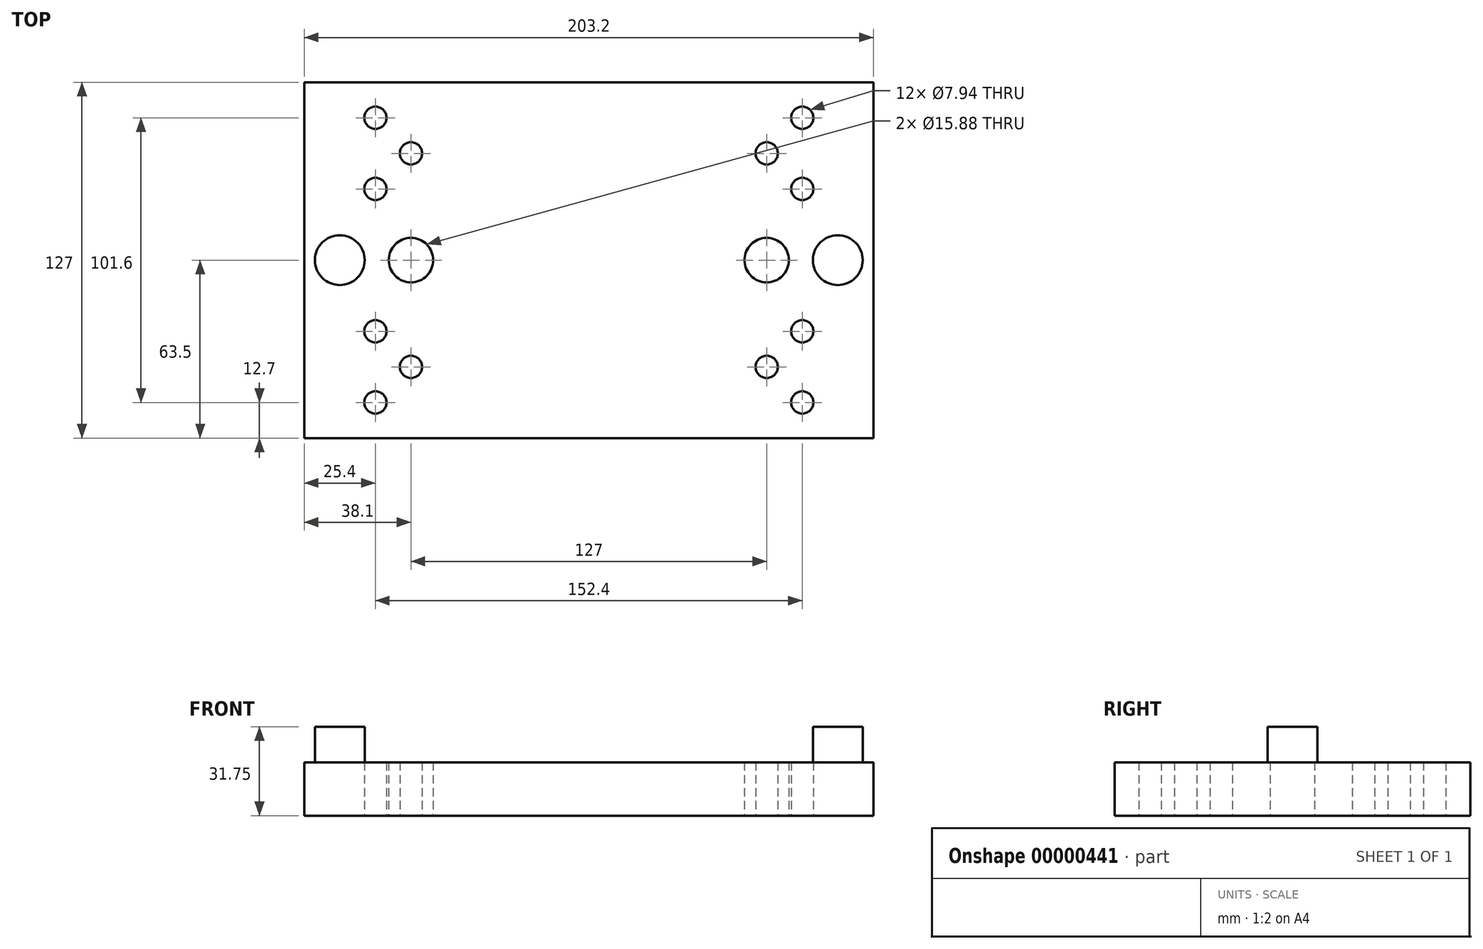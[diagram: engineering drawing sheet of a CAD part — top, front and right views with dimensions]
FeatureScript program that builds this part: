
annotation { "Feature Type Name" : "Feature", "Feature Type Description" : "" }
export const myFeature = defineFeature(function(context is Context, id is Id, definition is map)
    precondition{}
    {
        {
            var Q0;
            Q0=qCreatedBy(makeId("Top.planeOp"),FACE);
            var sketch = newSketch(context, id + "F0", { "sketchPlane" : qUnion([Q0])});
            skLineSegment(sketch, "E0.bottom", {"start": v(0, 0) * mm, "end": v(203.2, 0) * mm});
            skLineSegment(sketch, "E0.top", {"start": v(0, 127) * mm, "end": v(203.2, 127) * mm});
            skLineSegment(sketch, "E0.left", {"start": v(0, 0) * mm, "end": v(0, 127) * mm});
            skLineSegment(sketch, "E0.right", {"start": v(203.2, 0) * mm, "end": v(203.2, 127) * mm});
            skCircle(sketch, "E1", {"center": v(38.1, 63.5) * mm, "radius": 7.94 * mm});
            skCircle(sketch, "E2", {"center": v(165.1, 63.5) * mm, "radius": 7.94 * mm});
            skCircle(sketch, "E3", {"center": v(177.8, 114.3) * mm, "radius": 3.97 * mm});
            skCircle(sketch, "E4", {"center": v(165.1, 101.6) * mm, "radius": 3.97 * mm});
            skCircle(sketch, "E5", {"center": v(177.8, 88.9) * mm, "radius": 3.97 * mm});
            skCircle(sketch, "E6", {"center": v(177.8, 38.1) * mm, "radius": 3.97 * mm});
            skCircle(sketch, "E7", {"center": v(165.1, 25.4) * mm, "radius": 3.97 * mm});
            skCircle(sketch, "E8", {"center": v(177.8, 12.7) * mm, "radius": 3.97 * mm});
            skCircle(sketch, "E9", {"center": v(25.4, 38.1) * mm, "radius": 3.97 * mm});
            skCircle(sketch, "E10", {"center": v(38.1, 25.4) * mm, "radius": 3.97 * mm});
            skCircle(sketch, "E11", {"center": v(25.4, 12.7) * mm, "radius": 3.97 * mm});
            skCircle(sketch, "E12", {"center": v(25.4, 114.3) * mm, "radius": 3.97 * mm});
            skCircle(sketch, "E13", {"center": v(38.1, 101.6) * mm, "radius": 3.97 * mm});
            skCircle(sketch, "E14", {"center": v(25.4, 88.9) * mm, "radius": 3.97 * mm});
            skSolve(sketch);
        }
        {
            var Q0;
            Q0=makeQuery(id+"F0.imprint","IMPRINT",FACE,{"disambiguationData":[TD([[makeQuery(id+"F0.imprint","IMPRINT",EDGE,{"derivedFrom":sQuery(id+"F0.wireOp",EDGE,"E0.bottom")}),1.0]])]});
            extrude(context, id + "F1", {"entities" : qUnion([Q0]), "depth" : 19.05 * mm});
        }
        {
            var Q0;
            Q0=makeQuery(id+"F1.opExtrude","CAP_FACE",FACE,{"disambiguationData":[OSD([sQuery(id+"F0.wireOp",EDGE,"E0.bottom"),sQuery(id+"F0.wireOp",EDGE,"E0.top"),sQuery(id+"F0.wireOp",EDGE,"E0.left"),sQuery(id+"F0.wireOp",EDGE,"E0.right"),sQuery(id+"F0.wireOp",EDGE,"E1"),sQuery(id+"F0.wireOp",EDGE,"E2"),sQuery(id+"F0.wireOp",EDGE,"E3"),sQuery(id+"F0.wireOp",EDGE,"E4"),sQuery(id+"F0.wireOp",EDGE,"E5"),sQuery(id+"F0.wireOp",EDGE,"E6"),sQuery(id+"F0.wireOp",EDGE,"E7"),sQuery(id+"F0.wireOp",EDGE,"E8"),sQuery(id+"F0.wireOp",EDGE,"E9"),sQuery(id+"F0.wireOp",EDGE,"E10"),sQuery(id+"F0.wireOp",EDGE,"E11"),sQuery(id+"F0.wireOp",EDGE,"E12"),sQuery(id+"F0.wireOp",EDGE,"E13"),sQuery(id+"F0.wireOp",EDGE,"E14")])],"isStart":false});
            var sketch = newSketch(context, id + "F2", { "sketchPlane" : qUnion([Q0])});
            skCircle(sketch, "E15", {"center": v(12.7, 63.5) * mm, "radius": 8.9 * mm});
            skCircle(sketch, "E16", {"center": v(190.5, 63.5) * mm, "radius": 8.9 * mm});
            skSolve(sketch);
        }
        {
            var Q0;
            {Q0=qUnion([makeQuery(id+"F2.imprint","IMPRINT",FACE,{"disambiguationData":[TD([[makeQuery(id+"F2.imprint","IMPRINT",EDGE,{"derivedFrom":sQuery(id+"F2.wireOp",EDGE,"E15")}),1.0]])]}),makeQuery(id+"F2.imprint","IMPRINT",FACE,{"disambiguationData":[TD([[makeQuery(id+"F2.imprint","IMPRINT",EDGE,{"derivedFrom":sQuery(id+"F2.wireOp",EDGE,"E16")}),1.0]])]})]);}
            extrude(context, id + "F3", {"entities" : qUnion([Q0]), "operationType" : NewBodyOperationType.ADD, "depth" : 12.7 * mm});
        }
        {
            var Q0;
            Q0=makeQuery(id+"F1.opExtrude","CAP_FACE",FACE,{"disambiguationData":[OSD([sQuery(id+"F0.wireOp",EDGE,"E0.bottom"),sQuery(id+"F0.wireOp",EDGE,"E0.top"),sQuery(id+"F0.wireOp",EDGE,"E0.left"),sQuery(id+"F0.wireOp",EDGE,"E0.right"),sQuery(id+"F0.wireOp",EDGE,"E1"),sQuery(id+"F0.wireOp",EDGE,"E2"),sQuery(id+"F0.wireOp",EDGE,"E3"),sQuery(id+"F0.wireOp",EDGE,"E4"),sQuery(id+"F0.wireOp",EDGE,"E5"),sQuery(id+"F0.wireOp",EDGE,"E6"),sQuery(id+"F0.wireOp",EDGE,"E7"),sQuery(id+"F0.wireOp",EDGE,"E8"),sQuery(id+"F0.wireOp",EDGE,"E9"),sQuery(id+"F0.wireOp",EDGE,"E10"),sQuery(id+"F0.wireOp",EDGE,"E11"),sQuery(id+"F0.wireOp",EDGE,"E12"),sQuery(id+"F0.wireOp",EDGE,"E13"),sQuery(id+"F0.wireOp",EDGE,"E14")])],"isStart":false});
            var sketch = newSketch(context, id + "F4", { "sketchPlane" : qUnion([Q0])});
            skLineSegment(sketch, "E17.bottom", {"start": v(21.59, 137.16) * mm, "end": v(181.6, 137.16) * mm});
            skLineSegment(sketch, "E17.top", {"start": v(21.6, -10.16) * mm, "end": v(181.6, -10.16) * mm});
            skLineSegment(sketch, "E17.left", {"start": v(21.59, 137.16) * mm, "end": v(21.6, 68.42) * mm});
            skLineSegment(sketch, "E17.right", {"start": v(181.6, 137.16) * mm, "end": v(181.6, 68.42) * mm});
            skArc(sketch, "E18", {"start": v(21.6, 58.58) * mm, "mid": v(22.86, 63.5) * mm, "end": v(21.6, 68.42) * mm});
            skArc(sketch, "E19", {"start": v(181.6, 68.42) * mm, "mid": v(180.34, 63.5) * mm, "end": v(181.6, 58.58) * mm});
            skLineSegment(sketch, "E20.trimOffspring", {"start": v(21.6, 58.58) * mm, "end": v(21.6, -10.16) * mm});
            skLineSegment(sketch, "E21.trimOffspring", {"start": v(181.6, 58.58) * mm, "end": v(181.6, -10.16) * mm});
            skCircle(sketch, "E22.0", {"center": v(38.1, 101.6) * mm, "radius": 3.97 * mm});
            skCircle(sketch, "E23.0", {"center": v(165.1, 101.6) * mm, "radius": 3.97 * mm});
            skCircle(sketch, "E24.0", {"center": v(165.1, 63.5) * mm, "radius": 7.94 * mm});
            skCircle(sketch, "E25.0", {"center": v(165.1, 25.4) * mm, "radius": 3.97 * mm});
            skCircle(sketch, "E26.0", {"center": v(38.1, 25.4) * mm, "radius": 3.97 * mm});
            skCircle(sketch, "E27.0", {"center": v(38.1, 63.5) * mm, "radius": 7.94 * mm});
            skCircle(sketch, "E28", {"center": v(76.2, 113.5) * mm, "radius": 3.97 * mm});
            skCircle(sketch, "E29", {"center": v(76.2, 13.5) * mm, "radius": 3.97 * mm});
            skSolve(sketch);
        }
        {
            var Q0;
            {var subQ1=sQuery(id+"F4.wireOp",EDGE,"E17.right");var subQ3=sQuery(id+"F4.wireOp",EDGE,"E17.left");var subQ6=sQuery(id+"F4.wireOp",EDGE,"E17.bottom");var subQ8=sQuery(id+"F4.wireOp",EDGE,"E21.trimOffspring");var subQ10=sQuery(id+"F4.wireOp",EDGE,"E20.trimOffspring");var subQ13=sQuery(id+"F4.wireOp",EDGE,"E17.top");var subQ14=makeQuery(id+"F1.opExtrude","CAP_EDGE",EDGE,{"disambiguationData":[OSD([sQuery(id+"F0.wireOp",EDGE,"E14")])],"isStart":false});var subQ16=makeQuery(id+"F4.imprint","INTERSECT",VERTEX,{"disambiguationData":[OD(0.0)],"derivedFrom":[subQ14,subQ3]});var subQ18=makeQuery(id+"F1.opExtrude","CAP_EDGE",EDGE,{"disambiguationData":[OSD([sQuery(id+"F0.wireOp",EDGE,"E12")])],"isStart":false});var subQ20=makeQuery(id+"F4.imprint","INTERSECT",VERTEX,{"disambiguationData":[OD(0.0)],"derivedFrom":[subQ18,subQ3]});var subQ22=makeQuery(id+"F1.opExtrude","CAP_EDGE",EDGE,{"disambiguationData":[OSD([sQuery(id+"F0.wireOp",EDGE,"E9")])],"isStart":false});var subQ24=makeQuery(id+"F4.imprint","INTERSECT",VERTEX,{"disambiguationData":[OD(0.0)],"derivedFrom":[subQ22,subQ10]});var subQ26=makeQuery(id+"F1.opExtrude","CAP_EDGE",EDGE,{"disambiguationData":[OSD([sQuery(id+"F0.wireOp",EDGE,"E5")])],"isStart":false});var subQ28=makeQuery(id+"F4.imprint","INTERSECT",VERTEX,{"disambiguationData":[OD(0.0)],"derivedFrom":[subQ26,subQ1]});var subQ30=makeQuery(id+"F1.opExtrude","CAP_EDGE",EDGE,{"disambiguationData":[OSD([sQuery(id+"F0.wireOp",EDGE,"E8")])],"isStart":false});var subQ32=makeQuery(id+"F4.imprint","INTERSECT",VERTEX,{"disambiguationData":[OD(0.0)],"derivedFrom":[subQ30,subQ8]});var subQ34=makeQuery(id+"F1.opExtrude","CAP_EDGE",EDGE,{"disambiguationData":[OSD([sQuery(id+"F0.wireOp",EDGE,"E3")])],"isStart":false});var subQ36=makeQuery(id+"F4.imprint","INTERSECT",VERTEX,{"disambiguationData":[OD(0.0)],"derivedFrom":[subQ34,subQ1]});var subQ39=sQuery(id+"F4.wireOp",EDGE,"E18");var subQ40=makeQuery(id+"F1.opExtrude","CAP_EDGE",EDGE,{"disambiguationData":[OSD([sQuery(id+"F0.wireOp",EDGE,"E11")])],"isStart":false});var subQ42=makeQuery(id+"F4.imprint","INTERSECT",VERTEX,{"disambiguationData":[OD(0.0)],"derivedFrom":[subQ40,subQ10]});var subQ44=makeQuery(id+"F1.opExtrude","CAP_EDGE",EDGE,{"disambiguationData":[OSD([sQuery(id+"F0.wireOp",EDGE,"E6")])],"isStart":false});var subQ46=makeQuery(id+"F4.imprint","INTERSECT",VERTEX,{"disambiguationData":[OD(0.0)],"derivedFrom":[subQ44,subQ8]});Q0=qUnion([makeQuery(id+"F4.imprint","IMPRINT",FACE,{"disambiguationData":[TD([[makeQuery(id+"F4.imprint","IMPRINT",EDGE,{"derivedFrom":subQ6}),-1.0]])]}),makeQuery(id+"F4.imprint","IMPRINT",FACE,{"disambiguationData":[TD([[makeQuery(id+"F4.imprint","IMPRINT",EDGE,{"derivedFrom":subQ13}),1.0]])]}),makeQuery(id+"F4.imprint","IMPRINT",FACE,{"disambiguationData":[TD([[makeQuery(id+"F4.imprint","IMPRINT",EDGE,{"derivedFrom":subQ39}),-1.0]])]}),makeQuery(id+"F4.imprint","IMPRINT",FACE,{"disambiguationData":[TD([[makeQuery(id+"F4.imprint","IMPRINT",EDGE,{"disambiguationData":[TD([[subQ20,-1.0]])],"derivedFrom":subQ3}),1.0]])]}),makeQuery(id+"F4.imprint","IMPRINT",FACE,{"disambiguationData":[TD([[makeQuery(id+"F4.imprint","IMPRINT",EDGE,{"disambiguationData":[TD([[subQ16,-1.0]])],"derivedFrom":subQ3}),1.0]])]}),makeQuery(id+"F4.imprint","IMPRINT",FACE,{"disambiguationData":[TD([[makeQuery(id+"F4.imprint","IMPRINT",EDGE,{"disambiguationData":[TD([[subQ36,-1.0]])],"derivedFrom":subQ1}),-1.0]])]}),makeQuery(id+"F4.imprint","IMPRINT",FACE,{"disambiguationData":[TD([[makeQuery(id+"F4.imprint","IMPRINT",EDGE,{"disambiguationData":[TD([[subQ28,-1.0]])],"derivedFrom":subQ1}),-1.0]])]}),makeQuery(id+"F4.imprint","IMPRINT",FACE,{"disambiguationData":[TD([[makeQuery(id+"F4.imprint","IMPRINT",EDGE,{"disambiguationData":[TD([[subQ24,-1.0]])],"derivedFrom":subQ10}),1.0]])]}),makeQuery(id+"F4.imprint","IMPRINT",FACE,{"disambiguationData":[TD([[makeQuery(id+"F4.imprint","IMPRINT",EDGE,{"disambiguationData":[TD([[subQ42,-1.0]])],"derivedFrom":subQ10}),1.0]])]}),makeQuery(id+"F4.imprint","IMPRINT",FACE,{"disambiguationData":[TD([[makeQuery(id+"F4.imprint","IMPRINT",EDGE,{"disambiguationData":[TD([[subQ46,-1.0]])],"derivedFrom":subQ8}),-1.0]])]}),makeQuery(id+"F4.imprint","IMPRINT",FACE,{"disambiguationData":[TD([[makeQuery(id+"F4.imprint","IMPRINT",EDGE,{"disambiguationData":[TD([[subQ32,-1.0]])],"derivedFrom":subQ8}),-1.0]])]})]);}
            extrude(context, id + "F5", {"entities" : qUnion([Q0]), "depth" : 19.05 * mm});
        }
        {
            var Q0;
            Q0=makeQuery(id+"F5.opExtrude","CAP_FACE",FACE,{"disambiguationData":[OSD([sQuery(id+"F4.wireOp",EDGE,"E17.bottom"),sQuery(id+"F4.wireOp",EDGE,"E17.top"),sQuery(id+"F4.wireOp",EDGE,"E17.left"),sQuery(id+"F4.wireOp",EDGE,"E17.right"),sQuery(id+"F4.wireOp",EDGE,"E18"),sQuery(id+"F4.wireOp",EDGE,"E19"),sQuery(id+"F4.wireOp",EDGE,"E20.trimOffspring"),sQuery(id+"F4.wireOp",EDGE,"E21.trimOffspring"),sQuery(id+"F4.wireOp",EDGE,"E22.0"),sQuery(id+"F4.wireOp",EDGE,"E23.0"),sQuery(id+"F4.wireOp",EDGE,"E24.0"),sQuery(id+"F4.wireOp",EDGE,"E25.0"),sQuery(id+"F4.wireOp",EDGE,"E26.0"),sQuery(id+"F4.wireOp",EDGE,"E27.0"),sQuery(id+"F4.wireOp",EDGE,"E28"),sQuery(id+"F4.wireOp",EDGE,"E29")])],"isStart":false});
            var sketch = newSketch(context, id + "F6", { "sketchPlane" : qUnion([Q0])});
            skCircle(sketch, "E30", {"center": v(38.1, 63.5) * mm, "radius": 9.65 * mm});
            skCircle(sketch, "E31", {"center": v(165.1, 63.5) * mm, "radius": 9.65 * mm});
            skSolve(sketch);
        }
        {
            var Q0;
            {var subQ0=makeQuery(id+"F6.imprint","IMPRINT",EDGE,{"derivedFrom":makeQuery(id+"F5.opExtrude","CAP_EDGE",EDGE,{"disambiguationData":[OSD([sQuery(id+"F4.wireOp",EDGE,"E24.0")])],"isStart":false})});var subQ1=makeQuery(id+"F6.imprint","IMPRINT",EDGE,{"derivedFrom":makeQuery(id+"F5.opExtrude","CAP_EDGE",EDGE,{"disambiguationData":[OSD([sQuery(id+"F4.wireOp",EDGE,"E27.0")])],"isStart":false})});Q0=qUnion([makeQuery(id+"F6.imprint","IMPRINT",FACE,{"disambiguationData":[TD([[subQ0,1.0]])]}),makeQuery(id+"F6.imprint","IMPRINT",FACE,{"disambiguationData":[TD([[subQ1,1.0]])]}),makeQuery(id+"F6.imprint","IMPRINT",FACE,{"disambiguationData":[TD([[makeQuery(id+"F6.imprint","IMPRINT",EDGE,{"derivedFrom":sQuery(id+"F6.wireOp",EDGE,"E30")}),1.0]])]}),makeQuery(id+"F6.imprint","IMPRINT",FACE,{"disambiguationData":[TD([[makeQuery(id+"F6.imprint","IMPRINT",EDGE,{"derivedFrom":sQuery(id+"F6.wireOp",EDGE,"E31")}),1.0]])]})]);}
            extrude(context, id + "F7", {"entities" : qUnion([Q0]), "operationType" : NewBodyOperationType.REMOVE, "oppositeDirection" : true, "depth" : 1.9 * mm});
        }
        {
            var Q0;
            Q0=makeQuery(id+"F5.opExtrude","SWEPT_BODY",BODY,{"disambiguationData":[OSD([sQuery(id+"F4.wireOp",EDGE,"E17.bottom"),sQuery(id+"F4.wireOp",EDGE,"E17.top"),sQuery(id+"F4.wireOp",EDGE,"E17.left"),sQuery(id+"F4.wireOp",EDGE,"E17.right"),sQuery(id+"F4.wireOp",EDGE,"E18"),sQuery(id+"F4.wireOp",EDGE,"E19"),sQuery(id+"F4.wireOp",EDGE,"E20.trimOffspring"),sQuery(id+"F4.wireOp",EDGE,"E21.trimOffspring"),sQuery(id+"F4.wireOp",EDGE,"E22.0"),sQuery(id+"F4.wireOp",EDGE,"E23.0"),sQuery(id+"F4.wireOp",EDGE,"E24.0"),sQuery(id+"F4.wireOp",EDGE,"E25.0"),sQuery(id+"F4.wireOp",EDGE,"E26.0"),sQuery(id+"F4.wireOp",EDGE,"E27.0"),sQuery(id+"F4.wireOp",EDGE,"E28"),sQuery(id+"F4.wireOp",EDGE,"E29")])]});
            deleteBodies(context, id + "F8", {"entities" : qUnion([Q0])});
        }
    });
